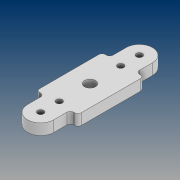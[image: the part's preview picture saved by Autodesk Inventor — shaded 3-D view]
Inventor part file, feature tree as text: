
AUTODESK INVENTOR PART (.ipt)
format: ipt  version: 2021 (Build 250183000, 183)  size: 143,360 bytes
history: native  units: mm
features: sketch x4, extrude x2, hole x2, fillet x1, projected_geometry x1
ambient origin geometry x8: Origin, YZ Plane, XZ Plane, XY Plane, X Axis, Y Axis, Z Axis, Center Point
bodies: Solid1 (feature_tree)
feature tree (10):
  extrude  "Extrusion1"  Depth=60.0mm
  hole  "Hole1"  [1 undecoded]
  fillet  "Fillet1"  Radius=10.0mm
  hole  "Hole2"  [1 undecoded]
  extrude  "Extrusion2"  Depth=10.0mm
  sketch  "Sketch1"  dims[d0=60.0mm d1=90.0mm]
  sketch  "Sketch2"  dims[d2=12.0mm d3=38.0mm d4=10.0mm d5=0.0mm]
  projected_geometry  "Projected Loop1"
  sketch  "Sketch3"  dims[d6=56.0mm]
  sketch  "Sketch4"  dims[d7=5.5mm d8=6.0mm d9=4.0mm d10=2.0mm d11=90.0deg d12=8.0mm d13=20.594885mm d14=3.0mm d15=5.5mm d16=6.0mm d17=4.0mm d18=2.0mm d19=90.0deg d20=8.0mm d21=20.594885mm d22=10.0mm d23=7.5mm d24=0.0mm]
note: 2 required parameter values undecoded (feature->parameter linkage not recoverable at this tier; creation-order binding heuristic only, values carry confidence <= 0.55)
